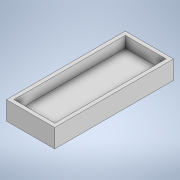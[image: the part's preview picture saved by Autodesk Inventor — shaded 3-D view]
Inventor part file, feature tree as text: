
AUTODESK INVENTOR PART (.ipt)
format: ipt  version: 2021 (Build 250183000, 183)  size: 112,640 bytes
history: native  units: in
note: dims shown in document units (in); Inventor stores cm internally (conversion verified against a paired STEP export)
features: extrude x2, sketch x2, projected_geometry x1
ambient origin geometry x8: Origin, YZ Plane, XZ Plane, XY Plane, X Axis, Y Axis, Z Axis, Center Point
bodies: Solid1 (feature_tree)
feature tree (5):
  extrude  "Extrusion1"  Depth=0.5118in
  extrude  "Extrusion2"  Depth=0.0394in
  sketch  "Sketch1"  dims[d0=1.2598in d1=0.5118in]
  sketch  "Sketch2"  dims[d2=0.0787in d3=0.0in d5=0.0394in d6=0.4331in d7=1.1811in d8=0.1181in d9=0.0in]
  projected_geometry  "Projected Loop1"
